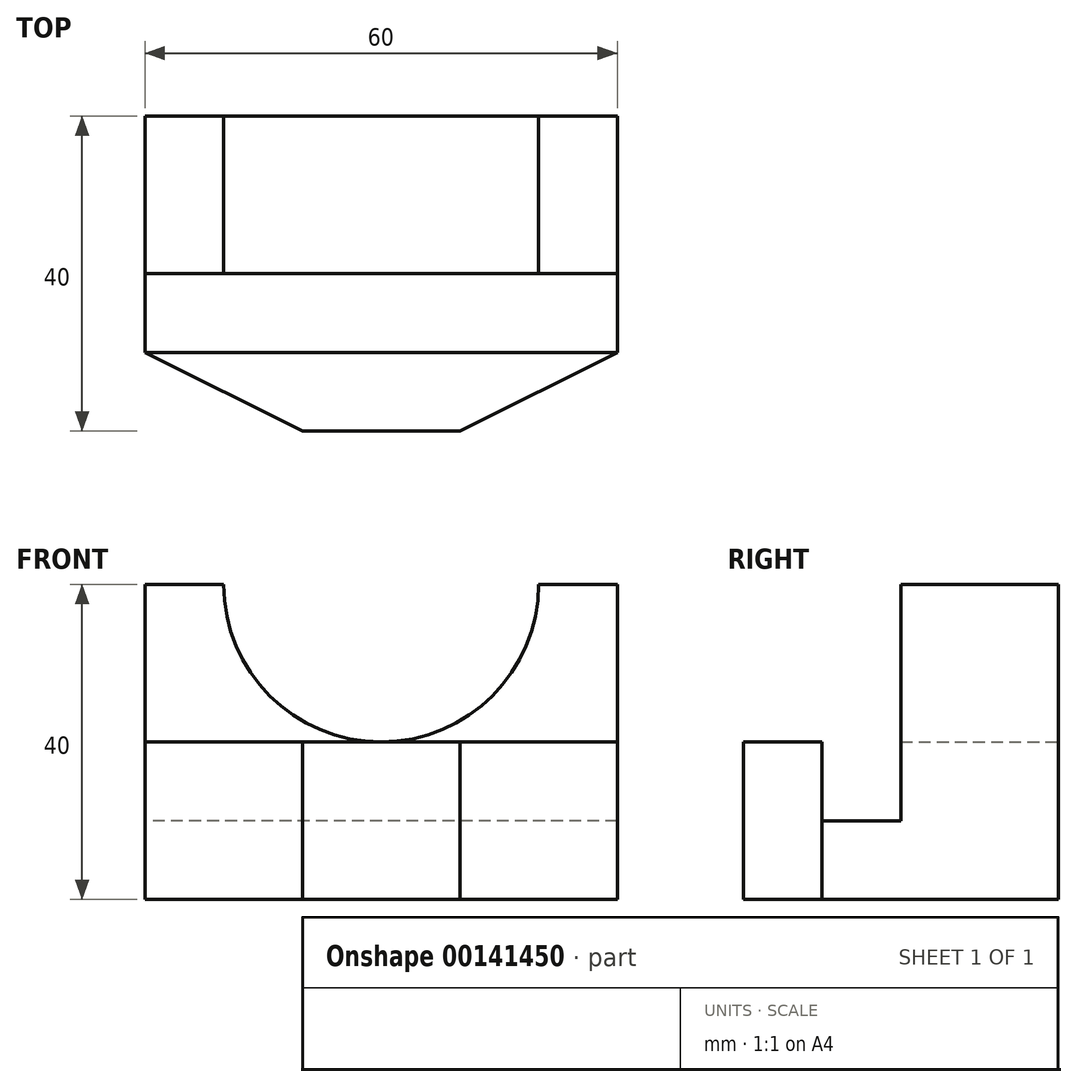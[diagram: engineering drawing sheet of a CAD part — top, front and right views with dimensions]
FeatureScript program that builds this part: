
annotation { "Feature Type Name" : "Feature", "Feature Type Description" : "" }
export const myFeature = defineFeature(function(context is Context, id is Id, definition is map)
    precondition{}
    {
        {
            var Q0;
            Q0=qCreatedBy(makeId("Top.planeOp"),FACE);
            var sketch = newSketch(context, id + "F0", { "sketchPlane" : qUnion([Q0])});
            skLineSegment(sketch, "E0", {"start": v(0, 0) * mm, "end": v(60, 0) * mm});
            skLineSegment(sketch, "E1", {"start": v(60, 0) * mm, "end": v(60, -20) * mm});
            skLineSegment(sketch, "E2", {"start": v(60, -20) * mm, "end": v(0, -20) * mm});
            skLineSegment(sketch, "E3", {"start": v(0, -20) * mm, "end": v(0, 0) * mm});
            skLineSegment(sketch, "E4", {"start": v(0, -20) * mm, "end": v(0, -30) * mm});
            skLineSegment(sketch, "E5", {"start": v(0, -30) * mm, "end": v(20, -40) * mm});
            skLineSegment(sketch, "E6", {"start": v(20, -40) * mm, "end": v(40, -40) * mm});
            skLineSegment(sketch, "E7", {"start": v(40, -40) * mm, "end": v(60, -30) * mm});
            skLineSegment(sketch, "E8", {"start": v(60, -30) * mm, "end": v(60, -20) * mm});
            skSolve(sketch);
        }
        {
            var Q0;
            Q0 = qSketchRegion(id + "F0", true);
            extrude(context, id + "F1", {"entities" : qUnion([Q0]), "depth" : 40 * mm});
        }
        {
            var Q0;
            Q0=qCreatedBy(makeId("Right.planeOp"),FACE);
            var sketch = newSketch(context, id + "F2", { "sketchPlane" : qUnion([Q0])});
            skLineSegment(sketch, "E9", {"start": v(-20, 40) * mm, "end": v(-20, 10) * mm});
            skLineSegment(sketch, "E10", {"start": v(-20, 10) * mm, "end": v(-30, 10) * mm});
            skLineSegment(sketch, "E11", {"start": v(-30, 10) * mm, "end": v(-30, 20) * mm});
            skLineSegment(sketch, "E12", {"start": v(-30, 20) * mm, "end": v(-40, 20) * mm});
            skLineSegment(sketch, "E13.0", {"start": v(0, 40) * mm, "end": v(-30, 40) * mm});
            skLineSegment(sketch, "E14.0", {"start": v(-30, 40) * mm, "end": v(-30, 0) * mm});
            skLineSegment(sketch, "E15.0", {"start": v(-40, 40) * mm, "end": v(-40, 0) * mm});
            skLineSegment(sketch, "E16.0", {"start": v(-40, 40) * mm, "end": v(-30, 40) * mm});
            skSolve(sketch);
        }
        {
            var Q0;
            Q0 = qSketchRegion(id + "F2", true);
            extrude(context, id + "F3", {"entities" : qUnion([Q0]), "operationType" : NewBodyOperationType.REMOVE, "depth" : 84.74 * mm});
        }
        {
            var Q0;
            Q0=qCreatedBy(makeId("Front.planeOp"),FACE);
            var sketch = newSketch(context, id + "F4", { "sketchPlane" : qUnion([Q0])});
            skLineSegment(sketch, "E17.0", {"start": v(60, 40) * mm, "end": v(0, 40) * mm});
            skArc(sketch, "E18", {"start": v(10, 40) * mm, "mid": v(30, 20) * mm, "end": v(50, 40) * mm});
            skSolve(sketch);
        }
        {
            var Q0;
            Q0 = qSketchRegion(id + "F4", true);
            extrude(context, id + "F5", {"entities" : qUnion([Q0]), "operationType" : NewBodyOperationType.REMOVE, "depth" : 25 * mm});
        }
    });
